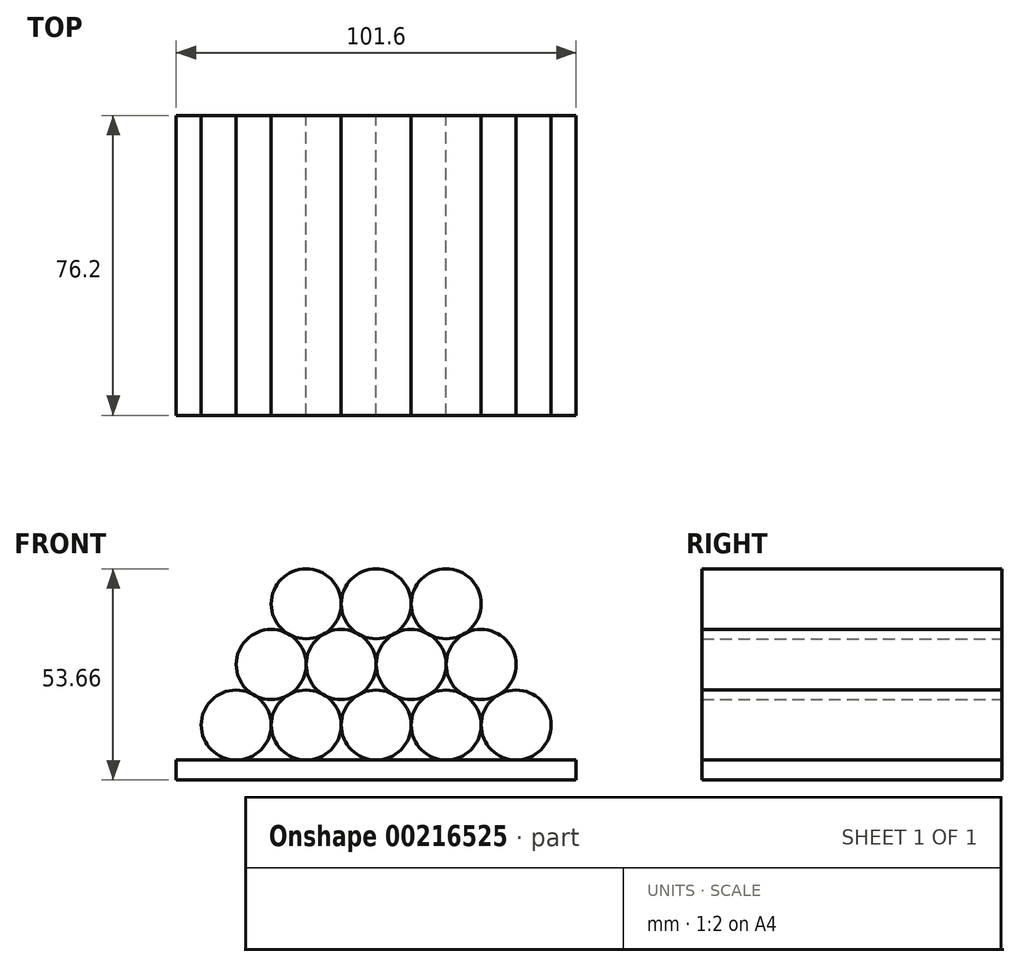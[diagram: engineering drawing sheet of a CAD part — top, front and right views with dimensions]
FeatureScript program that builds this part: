
annotation { "Feature Type Name" : "Feature", "Feature Type Description" : "" }
export const myFeature = defineFeature(function(context is Context, id is Id, definition is map)
    precondition{}
    {
        {
            var Q0;
            Q0=qCreatedBy(makeId("Front.planeOp"),FACE);
            var sketch = newSketch(context, id + "F0", { "sketchPlane" : qUnion([Q0])});
            skCircle(sketch, "E0", {"center": v(-26.67, 0) * mm, "radius": 8.9 * mm});
            skCircle(sketch, "E1", {"center": v(-8.9, 0) * mm, "radius": 8.9 * mm});
            skCircle(sketch, "E2", {"center": v(8.9, 0) * mm, "radius": 8.9 * mm});
            skCircle(sketch, "E3", {"center": v(26.67, 0) * mm, "radius": 8.9 * mm});
            skCircle(sketch, "E4", {"center": v(-17.78, 15.4) * mm, "radius": 8.9 * mm});
            skCircle(sketch, "E5", {"center": v(0, 15.4) * mm, "radius": 8.9 * mm});
            skCircle(sketch, "E6", {"center": v(17.78, 15.4) * mm, "radius": 8.9 * mm});
            skCircle(sketch, "E7", {"center": v(-35.56, -15.4) * mm, "radius": 8.9 * mm});
            skCircle(sketch, "E8", {"center": v(-17.78, -15.4) * mm, "radius": 8.9 * mm});
            skCircle(sketch, "E9", {"center": v(0, -15.4) * mm, "radius": 8.9 * mm});
            skCircle(sketch, "E10", {"center": v(17.78, -15.4) * mm, "radius": 8.9 * mm});
            skCircle(sketch, "E11", {"center": v(35.56, -15.4) * mm, "radius": 8.9 * mm});
            skLineSegment(sketch, "E12.bottom", {"start": v(-50.8, -24.29) * mm, "end": v(50.8, -24.29) * mm});
            skLineSegment(sketch, "E12.top", {"start": v(-50.8, -29.37) * mm, "end": v(50.8, -29.37) * mm});
            skLineSegment(sketch, "E12.left", {"start": v(-50.8, -24.29) * mm, "end": v(-50.8, -29.37) * mm});
            skLineSegment(sketch, "E12.right", {"start": v(50.8, -24.29) * mm, "end": v(50.8, -29.37) * mm});
            skSolve(sketch);
        }
        {
            var Q0;
            {var subQ0=sQuery(id+"F0.wireOp",EDGE,"E4");var subQ1=makeQuery(id+"F0.imprint","INTERSECT",VERTEX,{"derivedFrom":[sQuery(id+"F0.wireOp",EDGE,"E0"),subQ0]});Q0=makeQuery(id+"F0.imprint","IMPRINT",FACE,{"disambiguationData":[TD([[makeQuery(id+"F0.imprint","IMPRINT",EDGE,{"disambiguationData":[TD([[subQ1,1.0]])],"derivedFrom":subQ0}),1.0]])]});}
            var Q1;
            {var subQ0=sQuery(id+"F0.wireOp",EDGE,"E5");var subQ1=makeQuery(id+"F0.imprint","INTERSECT",VERTEX,{"derivedFrom":[sQuery(id+"F0.wireOp",EDGE,"E4"),subQ0]});Q1=makeQuery(id+"F0.imprint","IMPRINT",FACE,{"disambiguationData":[TD([[makeQuery(id+"F0.imprint","IMPRINT",EDGE,{"disambiguationData":[TD([[subQ1,1.0]])],"derivedFrom":subQ0}),1.0]])]});}
            var Q2;
            {var subQ0=sQuery(id+"F0.wireOp",EDGE,"E6");var subQ1=makeQuery(id+"F0.imprint","INTERSECT",VERTEX,{"derivedFrom":[sQuery(id+"F0.wireOp",EDGE,"E5"),subQ0]});Q2=makeQuery(id+"F0.imprint","IMPRINT",FACE,{"disambiguationData":[TD([[makeQuery(id+"F0.imprint","IMPRINT",EDGE,{"disambiguationData":[TD([[subQ1,-1.0]])],"derivedFrom":subQ0}),1.0]])]});}
            var Q3;
            {var subQ0=sQuery(id+"F0.wireOp",EDGE,"E3");var subQ1=makeQuery(id+"F0.imprint","INTERSECT",VERTEX,{"derivedFrom":[subQ0,sQuery(id+"F0.wireOp",EDGE,"E6")]});Q3=makeQuery(id+"F0.imprint","IMPRINT",FACE,{"disambiguationData":[TD([[makeQuery(id+"F0.imprint","IMPRINT",EDGE,{"disambiguationData":[TD([[subQ1,-1.0]])],"derivedFrom":subQ0}),1.0]])]});}
            var Q4;
            {var subQ0=sQuery(id+"F0.wireOp",EDGE,"E2");var subQ4=makeQuery(id+"F0.imprint","INTERSECT",VERTEX,{"derivedFrom":[subQ0,sQuery(id+"F0.wireOp",EDGE,"E6")]});Q4=makeQuery(id+"F0.imprint","IMPRINT",FACE,{"disambiguationData":[TD([[makeQuery(id+"F0.imprint","IMPRINT",EDGE,{"disambiguationData":[TD([[subQ4,1.0]])],"derivedFrom":subQ0}),1.0]])]});}
            var Q5;
            {var subQ0=sQuery(id+"F0.wireOp",EDGE,"E1");var subQ4=makeQuery(id+"F0.imprint","INTERSECT",VERTEX,{"derivedFrom":[subQ0,sQuery(id+"F0.wireOp",EDGE,"E5")]});Q5=makeQuery(id+"F0.imprint","IMPRINT",FACE,{"disambiguationData":[TD([[makeQuery(id+"F0.imprint","IMPRINT",EDGE,{"disambiguationData":[TD([[subQ4,1.0]])],"derivedFrom":subQ0}),1.0]])]});}
            var Q6;
            {var subQ0=sQuery(id+"F0.wireOp",EDGE,"E0");var subQ1=makeQuery(id+"F0.imprint","INTERSECT",VERTEX,{"derivedFrom":[subQ0,sQuery(id+"F0.wireOp",EDGE,"E4")]});Q6=makeQuery(id+"F0.imprint","IMPRINT",FACE,{"disambiguationData":[TD([[makeQuery(id+"F0.imprint","IMPRINT",EDGE,{"disambiguationData":[TD([[subQ1,1.0]])],"derivedFrom":subQ0}),1.0]])]});}
            var Q7;
            {var subQ0=sQuery(id+"F0.wireOp",EDGE,"E7");var subQ1=makeQuery(id+"F0.imprint","INTERSECT",VERTEX,{"derivedFrom":[sQuery(id+"F0.wireOp",EDGE,"E0"),subQ0]});Q7=makeQuery(id+"F0.imprint","IMPRINT",FACE,{"disambiguationData":[TD([[makeQuery(id+"F0.imprint","IMPRINT",EDGE,{"disambiguationData":[TD([[subQ1,1.0]])],"derivedFrom":subQ0}),1.0]])]});}
            var Q8;
            {var subQ0=sQuery(id+"F0.wireOp",EDGE,"E8");var subQ4=makeQuery(id+"F0.imprint","INTERSECT",VERTEX,{"derivedFrom":[sQuery(id+"F0.wireOp",EDGE,"E1"),subQ0]});Q8=makeQuery(id+"F0.imprint","IMPRINT",FACE,{"disambiguationData":[TD([[makeQuery(id+"F0.imprint","IMPRINT",EDGE,{"disambiguationData":[TD([[subQ4,1.0]])],"derivedFrom":subQ0}),1.0]])]});}
            var Q9;
            {var subQ0=sQuery(id+"F0.wireOp",EDGE,"E9");var subQ4=makeQuery(id+"F0.imprint","INTERSECT",VERTEX,{"derivedFrom":[sQuery(id+"F0.wireOp",EDGE,"E2"),subQ0]});Q9=makeQuery(id+"F0.imprint","IMPRINT",FACE,{"disambiguationData":[TD([[makeQuery(id+"F0.imprint","IMPRINT",EDGE,{"disambiguationData":[TD([[subQ4,1.0]])],"derivedFrom":subQ0}),1.0]])]});}
            var Q10;
            {var subQ0=sQuery(id+"F0.wireOp",EDGE,"E10");var subQ4=makeQuery(id+"F0.imprint","INTERSECT",VERTEX,{"derivedFrom":[sQuery(id+"F0.wireOp",EDGE,"E3"),subQ0]});Q10=makeQuery(id+"F0.imprint","IMPRINT",FACE,{"disambiguationData":[TD([[makeQuery(id+"F0.imprint","IMPRINT",EDGE,{"disambiguationData":[TD([[subQ4,1.0]])],"derivedFrom":subQ0}),1.0]])]});}
            var Q11;
            {var subQ0=sQuery(id+"F0.wireOp",EDGE,"E11");var subQ1=makeQuery(id+"F0.imprint","INTERSECT",VERTEX,{"derivedFrom":[sQuery(id+"F0.wireOp",EDGE,"E3"),subQ0]});Q11=makeQuery(id+"F0.imprint","IMPRINT",FACE,{"disambiguationData":[TD([[makeQuery(id+"F0.imprint","IMPRINT",EDGE,{"disambiguationData":[TD([[subQ1,-1.0]])],"derivedFrom":subQ0}),1.0]])]});}
            var Q12;
            Q12=makeQuery(id+"F0.imprint","IMPRINT",FACE,{"disambiguationData":[TD([[makeQuery(id+"F0.imprint","IMPRINT",EDGE,{"derivedFrom":sQuery(id+"F0.wireOp",EDGE,"E12.top")}),1.0]])]});
            var Q13;
            Q13=sQuery(id+"F0.wireOp",EDGE,"E5");
            var Q14;
            Q14=sQuery(id+"F0.wireOp",EDGE,"E6");
            var Q15;
            Q15=sQuery(id+"F0.wireOp",EDGE,"E12.bottom");
            var Q16;
            Q16=sQuery(id+"F0.wireOp",EDGE,"E1");
            var Q17;
            Q17=sQuery(id+"F0.wireOp",EDGE,"E3");
            var Q18;
            Q18=sQuery(id+"F0.wireOp",EDGE,"E4");
            var Q19;
            Q19=sQuery(id+"F0.wireOp",EDGE,"E11");
            var Q20;
            Q20=sQuery(id+"F0.wireOp",EDGE,"E8");
            var Q21;
            Q21=sQuery(id+"F0.wireOp",EDGE,"E2");
            var Q22;
            Q22=sQuery(id+"F0.wireOp",EDGE,"E12.top");
            var Q23;
            Q23=sQuery(id+"F0.wireOp",EDGE,"E0");
            var Q24;
            Q24=sQuery(id+"F0.wireOp",EDGE,"E9");
            var Q25;
            Q25=sQuery(id+"F0.wireOp",EDGE,"E10");
            var Q26;
            Q26=sQuery(id+"F0.wireOp",EDGE,"E7");
            var Q27;
            Q27=sQuery(id+"F0.wireOp",EDGE,"E12.left");
            var Q28;
            Q28=sQuery(id+"F0.wireOp",EDGE,"E12.right");
            extrude(context, id + "F1", {"entities" : qUnion([Q0, Q1, Q2, Q3, Q4, Q5, Q6, Q7, Q8, Q9, Q10, Q11, Q12]), "surfaceEntities" : qUnion([Q13, Q14, Q15, Q16, Q17, Q18, Q19, Q20, Q21, Q22, Q23, Q24, Q25, Q26, Q27, Q28]), "depth" : 76.2 * mm});
        }
    });
